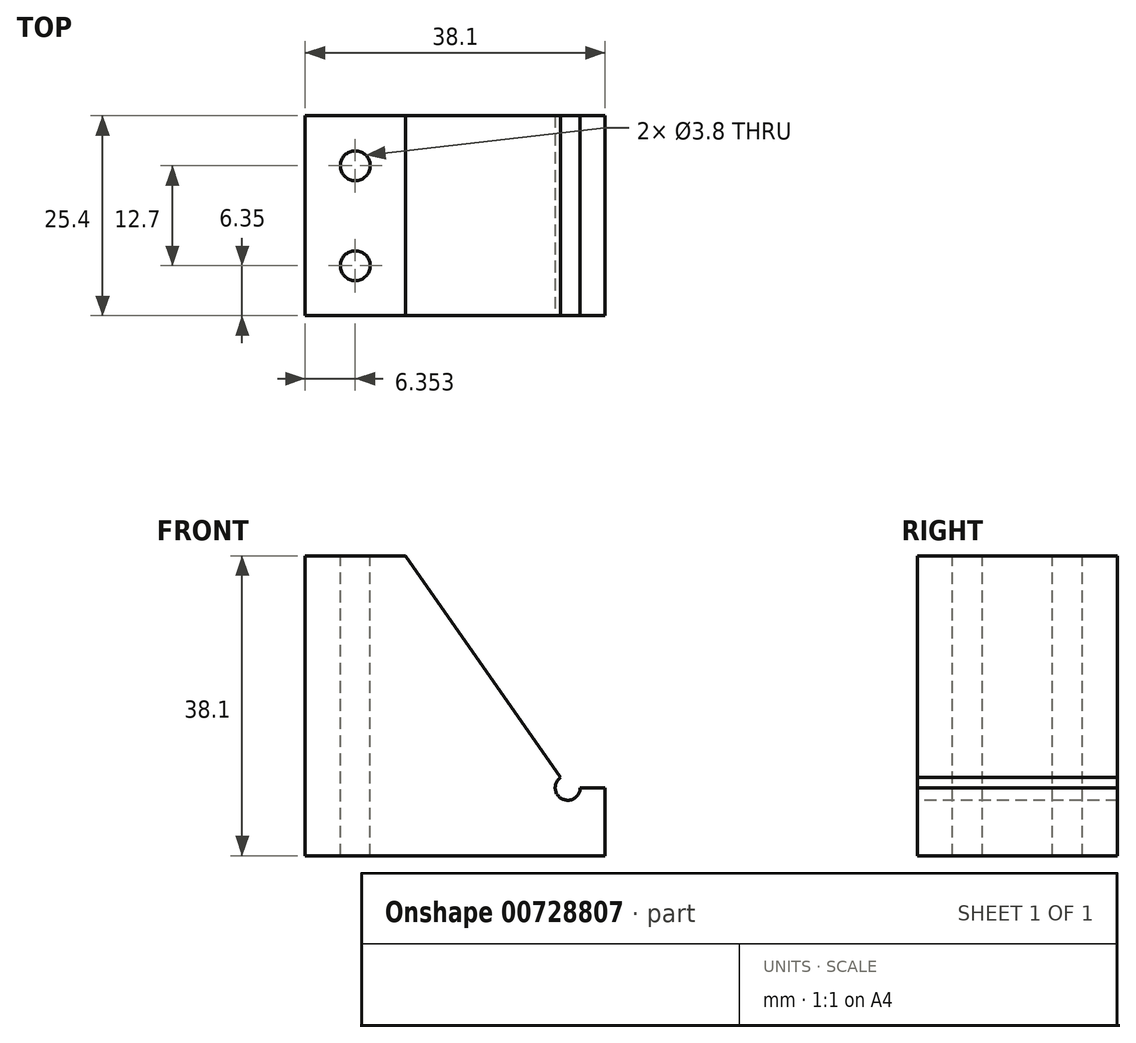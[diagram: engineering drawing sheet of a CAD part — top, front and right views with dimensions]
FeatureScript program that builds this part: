
annotation { "Feature Type Name" : "Feature", "Feature Type Description" : "" }
export const myFeature = defineFeature(function(context is Context, id is Id, definition is map)
    precondition{}
    {
        {
            var Q0;
            Q0=qCreatedBy(makeId("Front.planeOp"),FACE);
            var sketch = newSketch(context, id + "F0", { "sketchPlane" : qUnion([Q0])});
            skLineSegment(sketch, "E0", {"start": v(0, 0) * mm, "end": v(38.1, 0) * mm});
            skLineSegment(sketch, "E1", {"start": v(38.1, 0) * mm, "end": v(38.1, 8.64) * mm});
            skLineSegment(sketch, "E2", {"start": v(38.1, 8.64) * mm, "end": v(33.34, 8.64) * mm});
            skLineSegment(sketch, "E3", {"start": v(33.34, 8.64) * mm, "end": v(12.7, 38.1) * mm});
            skLineSegment(sketch, "E4", {"start": v(12.7, 38.1) * mm, "end": v(0, 38.1) * mm});
            skLineSegment(sketch, "E5", {"start": v(0, 38.1) * mm, "end": v(0, 0) * mm});
            skSolve(sketch);
        }
        {
            var Q0;
            Q0=makeQuery(id+"F0.imprint","IMPRINT",FACE,{"disambiguationData":[TD([[makeQuery(id+"F0.imprint","IMPRINT",EDGE,{"derivedFrom":sQuery(id+"F0.wireOp",EDGE,"E0")}),1.0]])]});
            extrude(context, id + "F1", {"entities" : qUnion([Q0]), "oppositeDirection" : true, "depth" : 25.4 * mm, "offsetDistance" : 25.4 * mm});
        }
        {
            var Q0;
            Q0=makeQuery(id+"F1.opExtrude","SWEPT_FACE",FACE,{"disambiguationData":[OSD([sQuery(id+"F0.wireOp",EDGE,"E4")])]});
            var sketch = newSketch(context, id + "F2", { "sketchPlane" : qUnion([Q0])});
            skCircle(sketch, "E6", {"center": v(6.35, 19.05) * mm, "radius": 2.75 * mm});
            skCircle(sketch, "E7", {"center": v(6.35, 6.35) * mm, "radius": 2.73 * mm});
            skSolve(sketch);
        }
        {
            var Q0;
            Q0=sQuery(id+"F2.wireOp",VERTEX,"E6.center");
            var Q1;
            Q1=sQuery(id+"F2.wireOp",VERTEX,"E7.center");
            var Q2;
            Q2=makeQuery(id+"F1.opExtrude","SWEPT_BODY",BODY,{"disambiguationData":[OSD([sQuery(id+"F0.wireOp",EDGE,"E0"),sQuery(id+"F0.wireOp",EDGE,"E1"),sQuery(id+"F0.wireOp",EDGE,"E2"),sQuery(id+"F0.wireOp",EDGE,"E3"),sQuery(id+"F0.wireOp",EDGE,"E4"),sQuery(id+"F0.wireOp",EDGE,"E5")])]});
            hole(context, id + "F3", {"style" : HoleStyle.SIMPLE, "endStyle" : HoleEndStyle.THROUGH, "standardTappedOrClearance" : lookupTablePath({ "standard" : "ANSI", "engagement" : "75%", "pitch" : "24 tpi", "size" : "#10", "type" : "Tapped" }), "standardBlindInLast" : lookupTablePath({ "standard" : "ANSI", "engagement" : "75%", "pitch" : "24 tpi", "size" : "#10", "type" : "Tapped" }), "holeDiameter" : 3.8 * mm, "majorDiameter" : 4.83 * mm, "showTappedDepth" : true, "isTappedThrough" : true, "tappedDepth" : 12.7 * mm, "tapClearance" : 3, "locations" : qUnion([Q0, Q1]), "scope" : qUnion([Q2])});
        }
        {
            var Q0;
            Q0=makeQuery(id+"F1.opExtrude","CAP_FACE",FACE,{"disambiguationData":[OSD([sQuery(id+"F0.wireOp",EDGE,"E0"),sQuery(id+"F0.wireOp",EDGE,"E1"),sQuery(id+"F0.wireOp",EDGE,"E2"),sQuery(id+"F0.wireOp",EDGE,"E3"),sQuery(id+"F0.wireOp",EDGE,"E4"),sQuery(id+"F0.wireOp",EDGE,"E5")])],"isStart":true});
            var sketch = newSketch(context, id + "F4", { "sketchPlane" : qUnion([Q0])});
            skPoint(sketch, "E8", {"position": v(33.34, 8.64) * mm});
            skSolve(sketch);
        }
        {
            var Q0;
            Q0=sQuery(id+"F4.wireOp",VERTEX,"E8");
            var Q1;
            Q1=makeQuery(id+"F1.opExtrude","SWEPT_BODY",BODY,{"disambiguationData":[OSD([sQuery(id+"F0.wireOp",EDGE,"E0"),sQuery(id+"F0.wireOp",EDGE,"E1"),sQuery(id+"F0.wireOp",EDGE,"E2"),sQuery(id+"F0.wireOp",EDGE,"E3"),sQuery(id+"F0.wireOp",EDGE,"E4"),sQuery(id+"F0.wireOp",EDGE,"E5")])]});
            hole(context, id + "F5", {"style" : HoleStyle.SIMPLE, "endStyle" : HoleEndStyle.THROUGH, "holeDiameter" : 3.17 * mm, "majorDiameter" : 6.35 * mm, "isTappedThrough" : true, "tappedDepth" : 12.7 * mm, "tapClearance" : 3, "locations" : qUnion([Q0]), "scope" : qUnion([Q1])});
        }
    });
